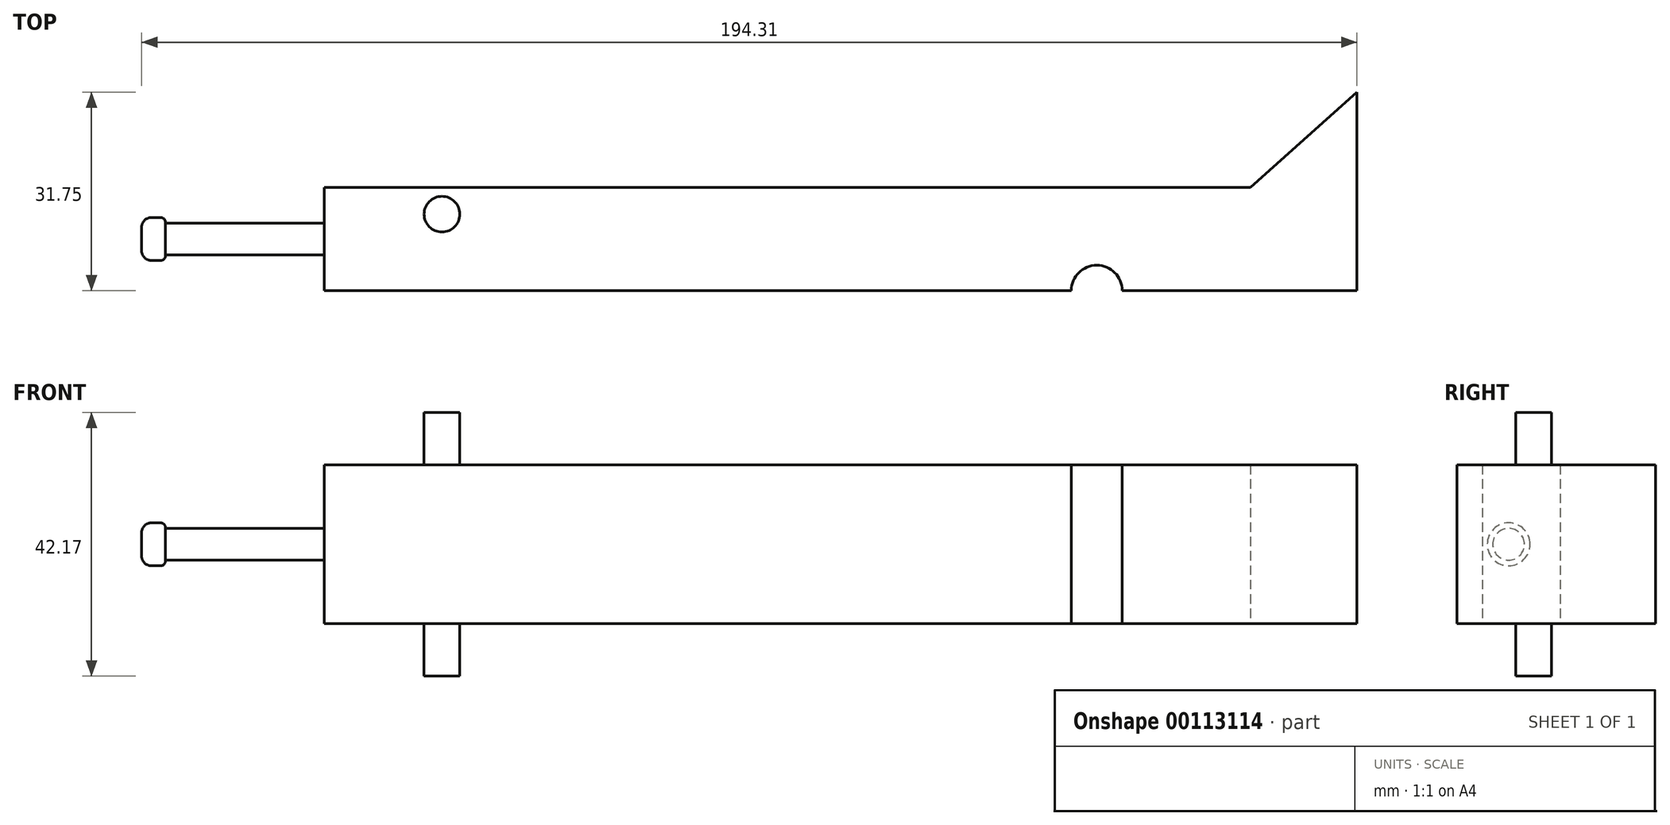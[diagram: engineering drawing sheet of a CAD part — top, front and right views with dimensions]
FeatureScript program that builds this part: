
annotation { "Feature Type Name" : "Feature", "Feature Type Description" : "" }
export const myFeature = defineFeature(function(context is Context, id is Id, definition is map)
    precondition{}
    {
        {
            var Q0;
            Q0=qCreatedBy(makeId("Front.planeOp"),FACE);
            var sketch = newSketch(context, id + "F0", { "sketchPlane" : qUnion([Q0])});
            skLineSegment(sketch, "E0.bottom", {"start": v(-65.26, 14.24) * mm, "end": v(99.84, 14.24) * mm});
            skLineSegment(sketch, "E0.top", {"start": v(-65.26, -11.16) * mm, "end": v(99.84, -11.16) * mm});
            skLineSegment(sketch, "E0.left", {"start": v(-65.26, 14.24) * mm, "end": v(-65.26, -11.16) * mm});
            skLineSegment(sketch, "E0.right", {"start": v(99.84, 14.24) * mm, "end": v(99.84, -11.16) * mm});
            skLineSegment(sketch, "E1", {"start": v(-65.26, 1.54) * mm, "end": v(99.84, 1.54) * mm, "construction": true});
            skSolve(sketch);
        }
        {
            var Q0;
            Q0=makeQuery(id+"F0.imprint","IMPRINT",FACE,{"disambiguationData":[TD([[makeQuery(id+"F0.imprint","IMPRINT",EDGE,{"derivedFrom":sQuery(id+"F0.wireOp",EDGE,"E0.bottom")}),-1.0]])]});
            var Q1;
            Q1=makeQuery(id+"F0.imprint","IMPRINT",FACE,{"disambiguationData":[TD([[makeQuery(id+"F0.imprint","IMPRINT",EDGE,{"derivedFrom":sQuery(id+"F0.wireOp",EDGE,"M2pgWJv9-Swt0-cPwD-kHqv-hG4U1bovwf7z")}),1.0]])]});
            extrude(context, id + "F1", {"entities" : qUnion([Q0, Q1]), "depth" : 16.5 * mm});
        }
        {
            var Q0;
            Q0=makeQuery(id+"F1.opExtrude","SWEPT_FACE",FACE,{"disambiguationData":[OSD([sQuery(id+"F0.wireOp",EDGE,"E0.top")])]});
            var sketch = newSketch(context, id + "F2", { "sketchPlane" : qUnion([Q0])});
            skLineSegment(sketch, "E2", {"start": v(82.8, 0) * mm, "end": v(99.84, 0) * mm});
            skLineSegment(sketch, "E3", {"start": v(99.84, 0) * mm, "end": v(99.84, -15.24) * mm});
            skLineSegment(sketch, "E4", {"start": v(99.84, -15.24) * mm, "end": v(82.8, 0) * mm});
            skSolve(sketch);
        }
        {
            var Q0;
            Q0=makeQuery(id+"F1.opExtrude","SWEPT_FACE",FACE,{"disambiguationData":[OSD([sQuery(id+"F0.wireOp",EDGE,"E0.top")])]});
            var sketch = newSketch(context, id + "F3", { "sketchPlane" : qUnion([Q0])});
            skLineSegment(sketch, "E5", {"start": v(-65.26, 4.28) * mm, "end": v(99.84, 4.28) * mm, "construction": true});
            skCircle(sketch, "E6", {"center": v(-46.46, 4.28) * mm, "radius": 2.86 * mm});
            skSolve(sketch);
        }
        {
            var Q0;
            Q0 = qSketchRegion(id + "F3", true);
            extrude(context, id + "F4", {"entities" : qUnion([Q0]), "operationType" : NewBodyOperationType.ADD, "depth" : 8.38 * mm, "hasSecondDirection" : true, "secondDirectionOppositeDirection" : true, "secondDirectionDepth" : 33.78 * mm});
        }
        {
            var Q0;
            Q0 = qSketchRegion(id + "F2", true);
            extrude(context, id + "F5", {"entities" : qUnion([Q0]), "operationType" : NewBodyOperationType.ADD, "oppositeDirection" : true, "depth" : 25.4 * mm});
        }
        {
            var Q0;
            Q0 = qSketchRegion(id + "F2", true);
            extrude(context, id + "F6", {"entities" : qUnion([Q0]), "operationType" : NewBodyOperationType.ADD, "oppositeDirection" : true, "depth" : 25.4 * mm});
        }
        {
            var Q0;
            Q0=makeQuery(id+"F5.boolean.opBoolean","MERGE",FACE,{"derivedFrom":[makeQuery(id+"F1.opExtrude","SWEPT_FACE",FACE,{"disambiguationData":[OSD([sQuery(id+"F0.wireOp",EDGE,"E0.top")])]}),makeQuery(id+"F5.opExtrude","CAP_FACE",FACE,{"disambiguationData":[OSD([sQuery(id+"F2.wireOp",EDGE,"E2"),sQuery(id+"F2.wireOp",EDGE,"E3"),sQuery(id+"F2.wireOp",EDGE,"E4")])],"isStart":true})]});
            var sketch = newSketch(context, id + "F7", { "sketchPlane" : qUnion([Q0])});
            skCircle(sketch, "E7", {"center": v(58.24, 16.51) * mm, "radius": 4.06 * mm});
            skSolve(sketch);
        }
        {
            var Q0;
            Q0 = qSketchRegion(id + "F7", true);
            extrude(context, id + "F8", {"entities" : qUnion([Q0]), "operationType" : NewBodyOperationType.REMOVE, "oppositeDirection" : true, "depth" : 25.4 * mm});
        }
        {
            var Q0;
            Q0=makeQuery(id+"F1.opExtrude","SWEPT_FACE",FACE,{"disambiguationData":[OSD([sQuery(id+"F0.wireOp",EDGE,"E0.left")])]});
            var sketch = newSketch(context, id + "F9", { "sketchPlane" : qUnion([Q0])});
            skLineSegment(sketch, "E8", {"start": v(8.26, 14.24) * mm, "end": v(8.26, -11.16) * mm, "construction": true});
            skPoint(sketch, "E9", {"position": v(8.26, 1.54) * mm});
            skCircle(sketch, "E10", {"center": v(8.26, 1.54) * mm, "radius": 2.54 * mm});
            skSolve(sketch);
        }
        {
            var Q0;
            Q0 = qSketchRegion(id + "F9", true);
            extrude(context, id + "F10", {"entities" : qUnion([Q0]), "operationType" : NewBodyOperationType.ADD, "depth" : 25.4 * mm});
        }
        {
            var Q0;
            Q0=makeQuery(id+"F10.opExtrude","CAP_FACE",FACE,{"disambiguationData":[OSD([sQuery(id+"F9.wireOp",EDGE,"E10")])],"isStart":false});
            var sketch = newSketch(context, id + "F11", { "sketchPlane" : qUnion([Q0])});
            skPoint(sketch, "E11", {"position": v(8.26, 1.54) * mm});
            skCircle(sketch, "E12", {"center": v(8.26, 1.54) * mm, "radius": 3.43 * mm});
            skSolve(sketch);
        }
        {
            var Q0;
            Q0 = qSketchRegion(id + "F11", true);
            extrude(context, id + "F12", {"entities" : qUnion([Q0]), "operationType" : NewBodyOperationType.ADD, "depth" : 3.8 * mm});
        }
        {
            var Q0;
            Q0=makeQuery(id+"F12.opExtrude","CAP_EDGE",EDGE,{"disambiguationData":[OSD([sQuery(id+"F11.wireOp",EDGE,"E12")])],"isStart":false});
            fillet(context, id + "F13", {"entities" : qUnion([Q0]), "radius" : 1.52 * mm, "tangentPropagation" : true, "allowEdgeOverflow" : false});
        }
        {
            var Q0;
            Q0=makeQuery(id+"F12.opExtrude","CAP_EDGE",EDGE,{"disambiguationData":[OSD([sQuery(id+"F11.wireOp",EDGE,"E12")])],"isStart":true});
            fillet(context, id + "F14", {"entities" : qUnion([Q0]), "radius" : 0.76 * mm, "tangentPropagation" : true, "allowEdgeOverflow" : false});
        }
    });
